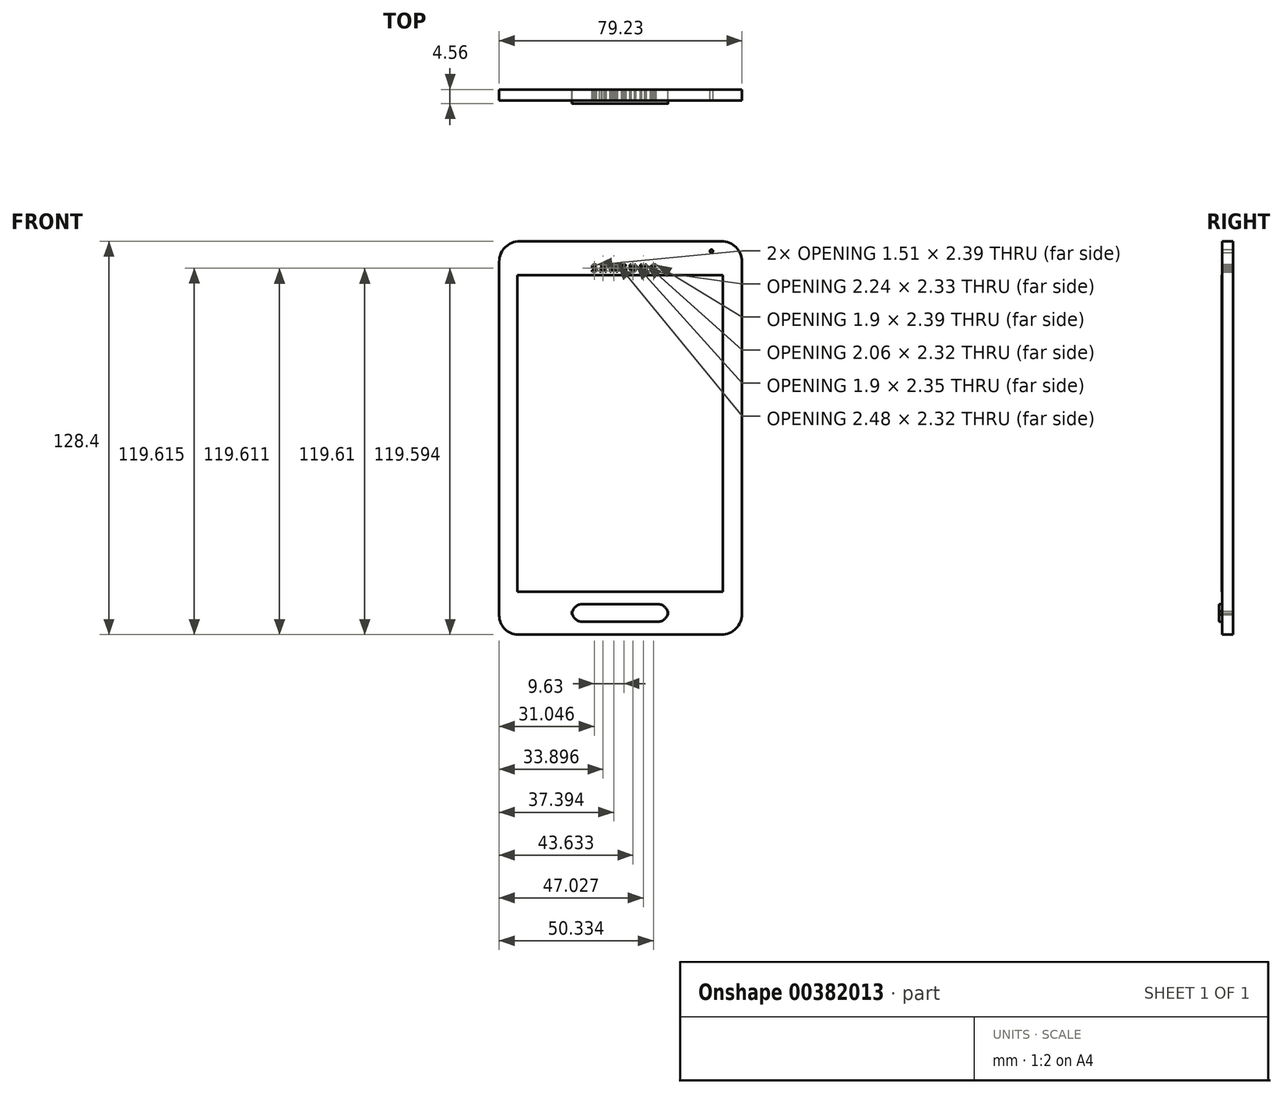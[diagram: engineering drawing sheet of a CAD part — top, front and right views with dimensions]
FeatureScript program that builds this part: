
annotation { "Feature Type Name" : "Feature", "Feature Type Description" : "" }
export const myFeature = defineFeature(function(context is Context, id is Id, definition is map)
    precondition{}
    {
        {
            var Q0;
            Q0=qCreatedBy(makeId("Front.planeOp"),FACE);
            var sketch = newSketch(context, id + "F0", { "sketchPlane" : qUnion([Q0])});
            skLineSegment(sketch, "E0.bottom", {"start": v(-53.86, 69.17) * mm, "end": v(11.97, 69.17) * mm});
            skLineSegment(sketch, "E0.top", {"start": v(-54.4, -59.23) * mm, "end": v(11.97, -59.23) * mm});
            skLineSegment(sketch, "E0.left", {"start": v(-60.56, 62.48) * mm, "end": v(-60.56, -53.06) * mm});
            skLineSegment(sketch, "E0.right", {"start": v(18.67, 62.48) * mm, "end": v(18.67, -52.53) * mm});
            skPoint(sketch, "E1.visualSharp", {"position": v(-60.56, 69.17) * mm});
            skArc(sketch, "E1.filletArc", {"start": v(-53.86, 69.17) * mm, "mid": v(-58.6, 67.21) * mm, "end": v(-60.56, 62.48) * mm});
            skPoint(sketch, "E2.visualSharp", {"position": v(18.67, 69.17) * mm});
            skArc(sketch, "E2.filletArc", {"start": v(18.67, 62.48) * mm, "mid": v(16.7, 67.21) * mm, "end": v(11.97, 69.17) * mm});
            skPoint(sketch, "E3.visualSharp", {"position": v(18.67, -59.23) * mm});
            skArc(sketch, "E3.filletArc", {"start": v(11.97, -59.23) * mm, "mid": v(16.7, -57.26) * mm, "end": v(18.67, -52.53) * mm});
            skPoint(sketch, "E4.visualSharp", {"position": v(-60.56, -59.23) * mm});
            skArc(sketch, "E4.filletArc", {"start": v(-60.56, -53.06) * mm, "mid": v(-58.75, -57.42) * mm, "end": v(-54.4, -59.23) * mm});
            skLineSegment(sketch, "E5", {"start": v(-54.67, 58.06) * mm, "end": v(12.46, 58.06) * mm});
            skLineSegment(sketch, "E6", {"start": v(12.46, 58.06) * mm, "end": v(12.46, -45.27) * mm});
            skLineSegment(sketch, "E7", {"start": v(12.46, -45.27) * mm, "end": v(-54.67, -45.27) * mm});
            skLineSegment(sketch, "E8", {"start": v(-54.67, -45.27) * mm, "end": v(-54.67, 58.06) * mm});
            skCircle(sketch, "E9", {"center": v(-47.07, 64.84) * mm, "radius": 1.65 * mm});
            skLineSegment(sketch, "E10.bottom", {"start": v(-28.87, 64.84) * mm, "end": v(-10.47, 64.84) * mm});
            skLineSegment(sketch, "E10.top", {"start": v(-28.77, 67.68) * mm, "end": v(-10.46, 67.68) * mm});
            skLineSegment(sketch, "E10.left", {"start": v(-29.78, 65.74) * mm, "end": v(-29.78, 66.67) * mm});
            skLineSegment(sketch, "E10.right", {"start": v(-9.55, 65.76) * mm, "end": v(-9.55, 66.78) * mm});
            skPoint(sketch, "E11.visualSharp", {"position": v(-29.78, 67.68) * mm});
            skArc(sketch, "E11.filletArc", {"start": v(-28.77, 67.68) * mm, "mid": v(-29.48, 67.39) * mm, "end": v(-29.78, 66.67) * mm});
            skPoint(sketch, "E12.visualSharp", {"position": v(-29.78, 64.84) * mm});
            skArc(sketch, "E12.filletArc", {"start": v(-29.78, 65.74) * mm, "mid": v(-29.51, 65.1) * mm, "end": v(-28.87, 64.84) * mm});
            skPoint(sketch, "E13.visualSharp", {"position": v(-9.55, 64.84) * mm});
            skArc(sketch, "E13.filletArc", {"start": v(-10.47, 64.84) * mm, "mid": v(-9.82, 65.1) * mm, "end": v(-9.55, 65.76) * mm});
            skPoint(sketch, "E14.visualSharp", {"position": v(-9.55, 67.68) * mm});
            skArc(sketch, "E14.filletArc", {"start": v(-9.55, 66.78) * mm, "mid": v(-9.82, 67.42) * mm, "end": v(-10.46, 67.68) * mm});
            skCircle(sketch, "E15", {"center": v(-3.77, 66.13) * mm, "radius": 1.09 * mm});
            skCircle(sketch, "E16", {"center": v(-0.62, 66.13) * mm, "radius": 1.1 * mm});
            skCircle(sketch, "E17", {"center": v(8.7, 65.95) * mm, "radius": 1.77 * mm});
            skCircle(sketch, "E18", {"center": v(8.7, 65.95) * mm, "radius": 0.51 * mm});
            skLineSegment(sketch, "E19.bottom", {"start": v(-33.35, -49.29) * mm, "end": v(-8.9, -49.29) * mm});
            skLineSegment(sketch, "E19.top", {"start": v(-33.35, -55.1) * mm, "end": v(-8.9, -55.1) * mm});
            skLineSegment(sketch, "E19.left", {"start": v(-36.82, -51.62) * mm, "end": v(-36.82, -52.76) * mm});
            skLineSegment(sketch, "E19.right", {"start": v(-5.44, -51.62) * mm, "end": v(-5.44, -52.76) * mm});
            skPoint(sketch, "E20.visualSharp", {"position": v(-36.82, -49.29) * mm});
            skArc(sketch, "E20.filletArc", {"start": v(-33.35, -49.29) * mm, "mid": v(-35.8, -50.3) * mm, "end": v(-36.82, -52.76) * mm});
            skPoint(sketch, "E21.visualSharp", {"position": v(-36.82, -55.1) * mm});
            skArc(sketch, "E21.filletArc", {"start": v(-36.82, -51.62) * mm, "mid": v(-35.8, -54.08) * mm, "end": v(-33.35, -55.1) * mm});
            skPoint(sketch, "E22.visualSharp", {"position": v(-5.44, -55.1) * mm});
            skArc(sketch, "E22.filletArc", {"start": v(-8.9, -55.1) * mm, "mid": v(-6.46, -54.08) * mm, "end": v(-5.44, -51.62) * mm});
            skPoint(sketch, "E23.visualSharp", {"position": v(-5.44, -49.29) * mm});
            skArc(sketch, "E23.filletArc", {"start": v(-5.44, -52.76) * mm, "mid": v(-6.46, -50.3) * mm, "end": v(-8.9, -49.29) * mm});
            skLineSegment(sketch, "E24.bottom", {"start": v(-55.14, -50.58) * mm, "end": v(-46.13, -50.58) * mm});
            skLineSegment(sketch, "E24.top", {"start": v(-55.14, -55.05) * mm, "end": v(-46.13, -55.05) * mm});
            skLineSegment(sketch, "E24.left", {"start": v(-55.14, -50.58) * mm, "end": v(-55.14, -55.05) * mm});
            skLineSegment(sketch, "E24.right", {"start": v(-46.13, -50.58) * mm, "end": v(-46.13, -55.05) * mm});
            skLineSegment(sketch, "E25", {"start": v(-50.67, -49.5) * mm, "end": v(-44.4, -49.5) * mm});
            skLineSegment(sketch, "E26", {"start": v(-44.4, -49.5) * mm, "end": v(-44.4, -54.04) * mm});
            skLineSegment(sketch, "E27", {"start": v(-44.4, -54.04) * mm, "end": v(-44.4, -49.5) * mm});
            skLineSegment(sketch, "E28", {"start": v(4.78, -54.93) * mm, "end": v(8.23, -54.93) * mm});
            skLineSegment(sketch, "E29", {"start": v(8.23, -54.93) * mm, "end": v(11.98, -54.93) * mm});
            skLineSegment(sketch, "E30", {"start": v(11.98, -54.93) * mm, "end": v(11.97, -52.53) * mm});
            skLineSegment(sketch, "E31", {"start": v(11.97, -50.8) * mm, "end": v(8.23, -50.8) * mm});
            skLineSegment(sketch, "E32", {"start": v(8.23, -50.8) * mm, "end": v(8.23, -49.07) * mm});
            skLineSegment(sketch, "E33", {"start": v(8.23, -49.07) * mm, "end": v(4.19, -50.54) * mm});
            skLineSegment(sketch, "E34", {"start": v(4.19, -50.54) * mm, "end": v(8.23, -52.53) * mm});
            skLineSegment(sketch, "E35", {"start": v(8.23, -52.53) * mm, "end": v(8.23, -50.8) * mm});
            skLineSegment(sketch, "E36", {"start": v(11.97, -50.8) * mm, "end": v(11.97, -52.53) * mm});
            skText(sketch, "E37", { "text": "S A M S U N G", "fontName": "OpenSans-Bold.ttf"});
            const initialGuessF0  = {"E37": [-0.03042, 0.05922, 1, 0, 0.00234]};
            skSetInitialGuess(sketch, initialGuessF0);
            skSolve(sketch);
        }
        {
            var Q0;
            Q0=makeQuery(id+"F0.imprint","IMPRINT",FACE,{"disambiguationData":[TD([[makeQuery(id+"F0.imprint","IMPRINT",EDGE,{"derivedFrom":sQuery(id+"F0.wireOp",EDGE,"E9")}),1.0]])]});
            var Q1;
            Q1=makeQuery(id+"F0.imprint","IMPRINT",FACE,{"disambiguationData":[TD([[makeQuery(id+"F0.imprint","IMPRINT",EDGE,{"derivedFrom":sQuery(id+"F0.wireOp",EDGE,"E10.bottom")}),1.0]])]});
            var Q2;
            {var subQ4=sQuery(id+"F0.wireOp",EDGE,"E19.bottom");Q2=makeQuery(id+"F0.imprint","IMPRINT",FACE,{"disambiguationData":[TD([[makeQuery(id+"F0.imprint","IMPRINT",EDGE,{"derivedFrom":subQ4}),-1.0]])]});}
            var Q3;
            Q3=makeQuery(id+"F0.imprint","IMPRINT",FACE,{"disambiguationData":[TD([[makeQuery(id+"F0.imprint","IMPRINT",EDGE,{"derivedFrom":sQuery(id+"F0.wireOp",EDGE,"E24.bottom")}),-1.0]])]});
            var Q4;
            Q4=makeQuery(id+"F0.imprint","IMPRINT",FACE,{"disambiguationData":[TD([[makeQuery(id+"F0.imprint","IMPRINT",EDGE,{"derivedFrom":sQuery(id+"F0.wireOp",EDGE,"E32")}),1.0]])]});
            var Q5;
            Q5=makeQuery(id+"F0.imprint","IMPRINT",FACE,{"disambiguationData":[TD([[makeQuery(id+"F0.imprint","IMPRINT",EDGE,{"derivedFrom":sQuery(id+"F0.wireOp",EDGE,"E15")}),1.0]])]});
            var Q6;
            Q6=makeQuery(id+"F0.imprint","IMPRINT",FACE,{"disambiguationData":[TD([[makeQuery(id+"F0.imprint","IMPRINT",EDGE,{"derivedFrom":sQuery(id+"F0.wireOp",EDGE,"E16")}),1.0]])]});
            var Q7;
            Q7=makeQuery(id+"F0.imprint","IMPRINT",FACE,{"disambiguationData":[TD([[makeQuery(id+"F0.imprint","IMPRINT",EDGE,{"derivedFrom":sQuery(id+"F0.wireOp",EDGE,"E17")}),1.0]])]});
            var Q8;
            Q8=makeQuery(id+"F0.imprint","IMPRINT",FACE,{"disambiguationData":[TD([[makeQuery(id+"F0.imprint","IMPRINT",EDGE,{"derivedFrom":sQuery(id+"F0.wireOp",EDGE,"E5")}),-1.0]])]});
            var Q9;
            Q9=makeQuery(id+"F0.imprint","IMPRINT",FACE,{"disambiguationData":[TD([[makeQuery(id+"F0.imprint","IMPRINT",EDGE,{"derivedFrom":sQuery(id+"F0.wireOp",EDGE,"E0.bottom")}),-1.0]])]});
            extrude(context, id + "F1", {"entities" : qUnion([Q0, Q1, Q2, Q3, Q4, Q5, Q6, Q7, Q8, Q9]), "depth" : 3.56 * mm});
        }
        {
            var Q0;
            Q0=makeQuery(id+"F1.opExtrude","CAP_FACE",FACE,{"disambiguationData":[OSD([sQuery(id+"F0.wireOp",EDGE,"E0.bottom"),sQuery(id+"F0.wireOp",EDGE,"E0.top"),sQuery(id+"F0.wireOp",EDGE,"E0.left"),sQuery(id+"F0.wireOp",EDGE,"E0.right"),sQuery(id+"F0.wireOp",EDGE,"E1.filletArc"),sQuery(id+"F0.wireOp",EDGE,"E2.filletArc"),sQuery(id+"F0.wireOp",EDGE,"E3.filletArc"),sQuery(id+"F0.wireOp",EDGE,"E4.filletArc"),sQuery(id+"F0.wireOp",EDGE,"E18"),sQuery(id+"F0.wireOp",EDGE,"E19.left"),sQuery(id+"F0.wireOp",EDGE,"E19.right"),sQuery(id+"F0.wireOp",EDGE,"E20.filletArc"),sQuery(id+"F0.wireOp",EDGE,"E21.filletArc"),sQuery(id+"F0.wireOp",EDGE,"E22.filletArc"),sQuery(id+"F0.wireOp",EDGE,"E23.filletArc"),sQuery(id+"F0.wireOp",EDGE,"E37.sketch_text.stroke-0"),sQuery(id+"F0.wireOp",EDGE,"E37.sketch_text.stroke-1"),sQuery(id+"F0.wireOp",EDGE,"E37.sketch_text.stroke-2"),sQuery(id+"F0.wireOp",EDGE,"E37.sketch_text.stroke-3"),sQuery(id+"F0.wireOp",EDGE,"E37.sketch_text.stroke-4"),sQuery(id+"F0.wireOp",EDGE,"E37.sketch_text.stroke-5"),sQuery(id+"F0.wireOp",EDGE,"E37.sketch_text.stroke-6"),sQuery(id+"F0.wireOp",EDGE,"E37.sketch_text.stroke-7"),sQuery(id+"F0.wireOp",EDGE,"E37.sketch_text.stroke-8"),sQuery(id+"F0.wireOp",EDGE,"E37.sketch_text.stroke-9"),sQuery(id+"F0.wireOp",EDGE,"E37.sketch_text.stroke-10"),sQuery(id+"F0.wireOp",EDGE,"E37.sketch_text.stroke-11"),sQuery(id+"F0.wireOp",EDGE,"E37.sketch_text.stroke-12"),sQuery(id+"F0.wireOp",EDGE,"E37.sketch_text.stroke-13"),sQuery(id+"F0.wireOp",EDGE,"E37.sketch_text.stroke-14"),sQuery(id+"F0.wireOp",EDGE,"E37.sketch_text.stroke-15"),sQuery(id+"F0.wireOp",EDGE,"E37.sketch_text.stroke-16"),sQuery(id+"F0.wireOp",EDGE,"E37.sketch_text.stroke-17"),sQuery(id+"F0.wireOp",EDGE,"E37.sketch_text.stroke-18"),sQuery(id+"F0.wireOp",EDGE,"E37.sketch_text.stroke-19"),sQuery(id+"F0.wireOp",EDGE,"E37.sketch_text.stroke-20"),sQuery(id+"F0.wireOp",EDGE,"E37.sketch_text.stroke-21"),sQuery(id+"F0.wireOp",EDGE,"E37.sketch_text.stroke-22"),sQuery(id+"F0.wireOp",EDGE,"E37.sketch_text.stroke-23"),sQuery(id+"F0.wireOp",EDGE,"E37.sketch_text.stroke-24"),sQuery(id+"F0.wireOp",EDGE,"E37.sketch_text.stroke-25"),sQuery(id+"F0.wireOp",EDGE,"E37.sketch_text.stroke-26"),sQuery(id+"F0.wireOp",EDGE,"E37.sketch_text.stroke-27"),sQuery(id+"F0.wireOp",EDGE,"E37.sketch_text.stroke-28"),sQuery(id+"F0.wireOp",EDGE,"E37.sketch_text.stroke-29"),sQuery(id+"F0.wireOp",EDGE,"E37.sketch_text.stroke-30"),sQuery(id+"F0.wireOp",EDGE,"E37.sketch_text.stroke-31"),sQuery(id+"F0.wireOp",EDGE,"E37.sketch_text.stroke-32"),sQuery(id+"F0.wireOp",EDGE,"E37.sketch_text.stroke-33"),sQuery(id+"F0.wireOp",EDGE,"E37.sketch_text.stroke-34"),sQuery(id+"F0.wireOp",EDGE,"E37.sketch_text.stroke-35"),sQuery(id+"F0.wireOp",EDGE,"E37.sketch_text.stroke-40"),sQuery(id+"F0.wireOp",EDGE,"E37.sketch_text.stroke-41"),sQuery(id+"F0.wireOp",EDGE,"E37.sketch_text.stroke-42"),sQuery(id+"F0.wireOp",EDGE,"E37.sketch_text.stroke-43"),sQuery(id+"F0.wireOp",EDGE,"E37.sketch_text.stroke-44"),sQuery(id+"F0.wireOp",EDGE,"E37.sketch_text.stroke-45"),sQuery(id+"F0.wireOp",EDGE,"E37.sketch_text.stroke-46"),sQuery(id+"F0.wireOp",EDGE,"E37.sketch_text.stroke-47"),sQuery(id+"F0.wireOp",EDGE,"E37.sketch_text.stroke-48"),sQuery(id+"F0.wireOp",EDGE,"E37.sketch_text.stroke-49"),sQuery(id+"F0.wireOp",EDGE,"E37.sketch_text.stroke-50"),sQuery(id+"F0.wireOp",EDGE,"E37.sketch_text.stroke-51"),sQuery(id+"F0.wireOp",EDGE,"E37.sketch_text.stroke-52"),sQuery(id+"F0.wireOp",EDGE,"E37.sketch_text.stroke-53"),sQuery(id+"F0.wireOp",EDGE,"E37.sketch_text.stroke-54"),sQuery(id+"F0.wireOp",EDGE,"E37.sketch_text.stroke-55"),sQuery(id+"F0.wireOp",EDGE,"E37.sketch_text.stroke-56"),sQuery(id+"F0.wireOp",EDGE,"E37.sketch_text.stroke-57"),sQuery(id+"F0.wireOp",EDGE,"E37.sketch_text.stroke-58"),sQuery(id+"F0.wireOp",EDGE,"E37.sketch_text.stroke-59"),sQuery(id+"F0.wireOp",EDGE,"E37.sketch_text.stroke-60"),sQuery(id+"F0.wireOp",EDGE,"E37.sketch_text.stroke-61"),sQuery(id+"F0.wireOp",EDGE,"E37.sketch_text.stroke-62"),sQuery(id+"F0.wireOp",EDGE,"E37.sketch_text.stroke-63"),sQuery(id+"F0.wireOp",EDGE,"E37.sketch_text.stroke-64"),sQuery(id+"F0.wireOp",EDGE,"E37.sketch_text.stroke-65"),sQuery(id+"F0.wireOp",EDGE,"E37.sketch_text.stroke-66"),sQuery(id+"F0.wireOp",EDGE,"E37.sketch_text.stroke-67"),sQuery(id+"F0.wireOp",EDGE,"E37.sketch_text.stroke-68"),sQuery(id+"F0.wireOp",EDGE,"E37.sketch_text.stroke-69"),sQuery(id+"F0.wireOp",EDGE,"E37.sketch_text.stroke-70"),sQuery(id+"F0.wireOp",EDGE,"E37.sketch_text.stroke-71"),sQuery(id+"F0.wireOp",EDGE,"E37.sketch_text.stroke-72"),sQuery(id+"F0.wireOp",EDGE,"E37.sketch_text.stroke-73"),sQuery(id+"F0.wireOp",EDGE,"E37.sketch_text.stroke-74"),sQuery(id+"F0.wireOp",EDGE,"E37.sketch_text.stroke-75"),sQuery(id+"F0.wireOp",EDGE,"E37.sketch_text.stroke-76"),sQuery(id+"F0.wireOp",EDGE,"E37.sketch_text.stroke-77"),sQuery(id+"F0.wireOp",EDGE,"E37.sketch_text.stroke-78"),sQuery(id+"F0.wireOp",EDGE,"E37.sketch_text.stroke-79"),sQuery(id+"F0.wireOp",EDGE,"E37.sketch_text.stroke-80"),sQuery(id+"F0.wireOp",EDGE,"E37.sketch_text.stroke-81"),sQuery(id+"F0.wireOp",EDGE,"E37.sketch_text.stroke-82"),sQuery(id+"F0.wireOp",EDGE,"E37.sketch_text.stroke-83"),sQuery(id+"F0.wireOp",EDGE,"E37.sketch_text.stroke-84"),sQuery(id+"F0.wireOp",EDGE,"E37.sketch_text.stroke-85"),sQuery(id+"F0.wireOp",EDGE,"E37.sketch_text.stroke-86"),sQuery(id+"F0.wireOp",EDGE,"E37.sketch_text.stroke-87"),sQuery(id+"F0.wireOp",EDGE,"E37.sketch_text.stroke-88"),sQuery(id+"F0.wireOp",EDGE,"E37.sketch_text.stroke-89"),sQuery(id+"F0.wireOp",EDGE,"E37.sketch_text.stroke-90"),sQuery(id+"F0.wireOp",EDGE,"E37.sketch_text.stroke-91"),sQuery(id+"F0.wireOp",EDGE,"E37.sketch_text.stroke-92"),sQuery(id+"F0.wireOp",EDGE,"E37.sketch_text.stroke-93"),sQuery(id+"F0.wireOp",EDGE,"E37.sketch_text.stroke-94"),sQuery(id+"F0.wireOp",EDGE,"E37.sketch_text.stroke-95"),sQuery(id+"F0.wireOp",EDGE,"E37.sketch_text.stroke-96"),sQuery(id+"F0.wireOp",EDGE,"E37.sketch_text.stroke-97"),sQuery(id+"F0.wireOp",EDGE,"E37.sketch_text.stroke-98"),sQuery(id+"F0.wireOp",EDGE,"E37.sketch_text.stroke-99"),sQuery(id+"F0.wireOp",EDGE,"E37.sketch_text.stroke-100"),sQuery(id+"F0.wireOp",EDGE,"E37.sketch_text.stroke-101"),sQuery(id+"F0.wireOp",EDGE,"E37.sketch_text.stroke-102"),sQuery(id+"F0.wireOp",EDGE,"E37.sketch_text.stroke-103"),sQuery(id+"F0.wireOp",EDGE,"E37.sketch_text.stroke-104"),sQuery(id+"F0.wireOp",EDGE,"E37.sketch_text.stroke-105"),sQuery(id+"F0.wireOp",EDGE,"E37.sketch_text.stroke-106"),sQuery(id+"F0.wireOp",EDGE,"E37.sketch_text.stroke-107"),sQuery(id+"F0.wireOp",EDGE,"E37.sketch_text.stroke-108"),sQuery(id+"F0.wireOp",EDGE,"E37.sketch_text.stroke-109"),sQuery(id+"F0.wireOp",EDGE,"E37.sketch_text.stroke-110"),sQuery(id+"F0.wireOp",EDGE,"E37.sketch_text.stroke-111"),sQuery(id+"F0.wireOp",EDGE,"E37.sketch_text.stroke-112"),sQuery(id+"F0.wireOp",EDGE,"E37.sketch_text.stroke-113"),sQuery(id+"F0.wireOp",EDGE,"E37.sketch_text.stroke-114"),sQuery(id+"F0.wireOp",EDGE,"E37.sketch_text.stroke-115"),sQuery(id+"F0.wireOp",EDGE,"E37.sketch_text.stroke-116"),sQuery(id+"F0.wireOp",EDGE,"E37.sketch_text.stroke-117"),sQuery(id+"F0.wireOp",EDGE,"E37.sketch_text.stroke-118"),sQuery(id+"F0.wireOp",EDGE,"E37.sketch_text.stroke-119"),sQuery(id+"F0.wireOp",EDGE,"E37.sketch_text.stroke-120"),sQuery(id+"F0.wireOp",EDGE,"E37.sketch_text.stroke-121"),sQuery(id+"F0.wireOp",EDGE,"E37.sketch_text.stroke-122"),sQuery(id+"F0.wireOp",EDGE,"E37.sketch_text.stroke-123"),sQuery(id+"F0.wireOp",EDGE,"E37.sketch_text.stroke-124"),sQuery(id+"F0.wireOp",EDGE,"E37.sketch_text.stroke-125"),sQuery(id+"F0.wireOp",EDGE,"E37.sketch_text.stroke-126"),sQuery(id+"F0.wireOp",EDGE,"E37.sketch_text.stroke-127"),sQuery(id+"F0.wireOp",EDGE,"E37.sketch_text.stroke-128"),sQuery(id+"F0.wireOp",EDGE,"E37.sketch_text.stroke-129"),sQuery(id+"F0.wireOp",EDGE,"E37.sketch_text.stroke-130"),sQuery(id+"F0.wireOp",EDGE,"E37.sketch_text.stroke-131"),sQuery(id+"F0.wireOp",EDGE,"E37.sketch_text.stroke-132"),sQuery(id+"F0.wireOp",EDGE,"E37.sketch_text.stroke-133"),sQuery(id+"F0.wireOp",EDGE,"E37.sketch_text.stroke-134")])],"isStart":false});
            var sketch = newSketch(context, id + "F2", { "sketchPlane" : qUnion([Q0])});
            skLineSegment(sketch, "E38.bottom", {"start": v(-33.35, -49.29) * mm, "end": v(-8.9, -49.29) * mm});
            skLineSegment(sketch, "E38.top", {"start": v(-33.35, -55.1) * mm, "end": v(-8.9, -55.1) * mm});
            skLineSegment(sketch, "E38.left", {"start": v(-36.82, -51.62) * mm, "end": v(-36.82, -52.76) * mm});
            skLineSegment(sketch, "E38.right", {"start": v(-5.44, -51.62) * mm, "end": v(-5.44, -52.76) * mm});
            skPoint(sketch, "E39.visualSharp", {"position": v(-36.82, -49.29) * mm});
            skArc(sketch, "E39.filletArc", {"start": v(-33.35, -49.29) * mm, "mid": v(-35.8, -50.3) * mm, "end": v(-36.82, -52.76) * mm});
            skPoint(sketch, "E40.visualSharp", {"position": v(-36.82, -55.1) * mm});
            skArc(sketch, "E40.filletArc", {"start": v(-36.82, -51.62) * mm, "mid": v(-35.8, -54.08) * mm, "end": v(-33.35, -55.1) * mm});
            skPoint(sketch, "E41.visualSharp", {"position": v(-5.44, -55.1) * mm});
            skArc(sketch, "E41.filletArc", {"start": v(-8.9, -55.1) * mm, "mid": v(-6.46, -54.08) * mm, "end": v(-5.44, -51.62) * mm});
            skPoint(sketch, "E42.visualSharp", {"position": v(-5.44, -49.29) * mm});
            skArc(sketch, "E42.filletArc", {"start": v(-5.44, -52.76) * mm, "mid": v(-6.46, -50.3) * mm, "end": v(-8.9, -49.29) * mm});
            skSolve(sketch);
        }
        {
            var Q0;
            Q0 = qSketchRegion(id + "F2", true);
            extrude(context, id + "F3", {"entities" : qUnion([Q0]), "depth" : 1 * mm});
        }
        {
            var Q0;
            Q0=makeQuery(id+"F1.opExtrude","CAP_FACE",FACE,{"disambiguationData":[OSD([sQuery(id+"F0.wireOp",EDGE,"E0.bottom"),sQuery(id+"F0.wireOp",EDGE,"E0.top"),sQuery(id+"F0.wireOp",EDGE,"E0.left"),sQuery(id+"F0.wireOp",EDGE,"E0.right"),sQuery(id+"F0.wireOp",EDGE,"E1.filletArc"),sQuery(id+"F0.wireOp",EDGE,"E2.filletArc"),sQuery(id+"F0.wireOp",EDGE,"E3.filletArc"),sQuery(id+"F0.wireOp",EDGE,"E4.filletArc"),sQuery(id+"F0.wireOp",EDGE,"E18"),sQuery(id+"F0.wireOp",EDGE,"E19.left"),sQuery(id+"F0.wireOp",EDGE,"E19.right"),sQuery(id+"F0.wireOp",EDGE,"E20.filletArc"),sQuery(id+"F0.wireOp",EDGE,"E21.filletArc"),sQuery(id+"F0.wireOp",EDGE,"E22.filletArc"),sQuery(id+"F0.wireOp",EDGE,"E23.filletArc"),sQuery(id+"F0.wireOp",EDGE,"E37.sketch_text.stroke-0"),sQuery(id+"F0.wireOp",EDGE,"E37.sketch_text.stroke-1"),sQuery(id+"F0.wireOp",EDGE,"E37.sketch_text.stroke-2"),sQuery(id+"F0.wireOp",EDGE,"E37.sketch_text.stroke-3"),sQuery(id+"F0.wireOp",EDGE,"E37.sketch_text.stroke-4"),sQuery(id+"F0.wireOp",EDGE,"E37.sketch_text.stroke-5"),sQuery(id+"F0.wireOp",EDGE,"E37.sketch_text.stroke-6"),sQuery(id+"F0.wireOp",EDGE,"E37.sketch_text.stroke-7"),sQuery(id+"F0.wireOp",EDGE,"E37.sketch_text.stroke-8"),sQuery(id+"F0.wireOp",EDGE,"E37.sketch_text.stroke-9"),sQuery(id+"F0.wireOp",EDGE,"E37.sketch_text.stroke-10"),sQuery(id+"F0.wireOp",EDGE,"E37.sketch_text.stroke-11"),sQuery(id+"F0.wireOp",EDGE,"E37.sketch_text.stroke-12"),sQuery(id+"F0.wireOp",EDGE,"E37.sketch_text.stroke-13"),sQuery(id+"F0.wireOp",EDGE,"E37.sketch_text.stroke-14"),sQuery(id+"F0.wireOp",EDGE,"E37.sketch_text.stroke-15"),sQuery(id+"F0.wireOp",EDGE,"E37.sketch_text.stroke-16"),sQuery(id+"F0.wireOp",EDGE,"E37.sketch_text.stroke-17"),sQuery(id+"F0.wireOp",EDGE,"E37.sketch_text.stroke-18"),sQuery(id+"F0.wireOp",EDGE,"E37.sketch_text.stroke-19"),sQuery(id+"F0.wireOp",EDGE,"E37.sketch_text.stroke-20"),sQuery(id+"F0.wireOp",EDGE,"E37.sketch_text.stroke-21"),sQuery(id+"F0.wireOp",EDGE,"E37.sketch_text.stroke-22"),sQuery(id+"F0.wireOp",EDGE,"E37.sketch_text.stroke-23"),sQuery(id+"F0.wireOp",EDGE,"E37.sketch_text.stroke-24"),sQuery(id+"F0.wireOp",EDGE,"E37.sketch_text.stroke-25"),sQuery(id+"F0.wireOp",EDGE,"E37.sketch_text.stroke-26"),sQuery(id+"F0.wireOp",EDGE,"E37.sketch_text.stroke-27"),sQuery(id+"F0.wireOp",EDGE,"E37.sketch_text.stroke-28"),sQuery(id+"F0.wireOp",EDGE,"E37.sketch_text.stroke-29"),sQuery(id+"F0.wireOp",EDGE,"E37.sketch_text.stroke-30"),sQuery(id+"F0.wireOp",EDGE,"E37.sketch_text.stroke-31"),sQuery(id+"F0.wireOp",EDGE,"E37.sketch_text.stroke-32"),sQuery(id+"F0.wireOp",EDGE,"E37.sketch_text.stroke-33"),sQuery(id+"F0.wireOp",EDGE,"E37.sketch_text.stroke-34"),sQuery(id+"F0.wireOp",EDGE,"E37.sketch_text.stroke-35"),sQuery(id+"F0.wireOp",EDGE,"E37.sketch_text.stroke-40"),sQuery(id+"F0.wireOp",EDGE,"E37.sketch_text.stroke-41"),sQuery(id+"F0.wireOp",EDGE,"E37.sketch_text.stroke-42"),sQuery(id+"F0.wireOp",EDGE,"E37.sketch_text.stroke-43"),sQuery(id+"F0.wireOp",EDGE,"E37.sketch_text.stroke-44"),sQuery(id+"F0.wireOp",EDGE,"E37.sketch_text.stroke-45"),sQuery(id+"F0.wireOp",EDGE,"E37.sketch_text.stroke-46"),sQuery(id+"F0.wireOp",EDGE,"E37.sketch_text.stroke-47"),sQuery(id+"F0.wireOp",EDGE,"E37.sketch_text.stroke-48"),sQuery(id+"F0.wireOp",EDGE,"E37.sketch_text.stroke-49"),sQuery(id+"F0.wireOp",EDGE,"E37.sketch_text.stroke-50"),sQuery(id+"F0.wireOp",EDGE,"E37.sketch_text.stroke-51"),sQuery(id+"F0.wireOp",EDGE,"E37.sketch_text.stroke-52"),sQuery(id+"F0.wireOp",EDGE,"E37.sketch_text.stroke-53"),sQuery(id+"F0.wireOp",EDGE,"E37.sketch_text.stroke-54"),sQuery(id+"F0.wireOp",EDGE,"E37.sketch_text.stroke-55"),sQuery(id+"F0.wireOp",EDGE,"E37.sketch_text.stroke-56"),sQuery(id+"F0.wireOp",EDGE,"E37.sketch_text.stroke-57"),sQuery(id+"F0.wireOp",EDGE,"E37.sketch_text.stroke-58"),sQuery(id+"F0.wireOp",EDGE,"E37.sketch_text.stroke-59"),sQuery(id+"F0.wireOp",EDGE,"E37.sketch_text.stroke-60"),sQuery(id+"F0.wireOp",EDGE,"E37.sketch_text.stroke-61"),sQuery(id+"F0.wireOp",EDGE,"E37.sketch_text.stroke-62"),sQuery(id+"F0.wireOp",EDGE,"E37.sketch_text.stroke-63"),sQuery(id+"F0.wireOp",EDGE,"E37.sketch_text.stroke-64"),sQuery(id+"F0.wireOp",EDGE,"E37.sketch_text.stroke-65"),sQuery(id+"F0.wireOp",EDGE,"E37.sketch_text.stroke-66"),sQuery(id+"F0.wireOp",EDGE,"E37.sketch_text.stroke-67"),sQuery(id+"F0.wireOp",EDGE,"E37.sketch_text.stroke-68"),sQuery(id+"F0.wireOp",EDGE,"E37.sketch_text.stroke-69"),sQuery(id+"F0.wireOp",EDGE,"E37.sketch_text.stroke-70"),sQuery(id+"F0.wireOp",EDGE,"E37.sketch_text.stroke-71"),sQuery(id+"F0.wireOp",EDGE,"E37.sketch_text.stroke-72"),sQuery(id+"F0.wireOp",EDGE,"E37.sketch_text.stroke-73"),sQuery(id+"F0.wireOp",EDGE,"E37.sketch_text.stroke-74"),sQuery(id+"F0.wireOp",EDGE,"E37.sketch_text.stroke-75"),sQuery(id+"F0.wireOp",EDGE,"E37.sketch_text.stroke-76"),sQuery(id+"F0.wireOp",EDGE,"E37.sketch_text.stroke-77"),sQuery(id+"F0.wireOp",EDGE,"E37.sketch_text.stroke-78"),sQuery(id+"F0.wireOp",EDGE,"E37.sketch_text.stroke-79"),sQuery(id+"F0.wireOp",EDGE,"E37.sketch_text.stroke-80"),sQuery(id+"F0.wireOp",EDGE,"E37.sketch_text.stroke-81"),sQuery(id+"F0.wireOp",EDGE,"E37.sketch_text.stroke-82"),sQuery(id+"F0.wireOp",EDGE,"E37.sketch_text.stroke-83"),sQuery(id+"F0.wireOp",EDGE,"E37.sketch_text.stroke-84"),sQuery(id+"F0.wireOp",EDGE,"E37.sketch_text.stroke-85"),sQuery(id+"F0.wireOp",EDGE,"E37.sketch_text.stroke-86"),sQuery(id+"F0.wireOp",EDGE,"E37.sketch_text.stroke-87"),sQuery(id+"F0.wireOp",EDGE,"E37.sketch_text.stroke-88"),sQuery(id+"F0.wireOp",EDGE,"E37.sketch_text.stroke-89"),sQuery(id+"F0.wireOp",EDGE,"E37.sketch_text.stroke-90"),sQuery(id+"F0.wireOp",EDGE,"E37.sketch_text.stroke-91"),sQuery(id+"F0.wireOp",EDGE,"E37.sketch_text.stroke-92"),sQuery(id+"F0.wireOp",EDGE,"E37.sketch_text.stroke-93"),sQuery(id+"F0.wireOp",EDGE,"E37.sketch_text.stroke-94"),sQuery(id+"F0.wireOp",EDGE,"E37.sketch_text.stroke-95"),sQuery(id+"F0.wireOp",EDGE,"E37.sketch_text.stroke-96"),sQuery(id+"F0.wireOp",EDGE,"E37.sketch_text.stroke-97"),sQuery(id+"F0.wireOp",EDGE,"E37.sketch_text.stroke-98"),sQuery(id+"F0.wireOp",EDGE,"E37.sketch_text.stroke-99"),sQuery(id+"F0.wireOp",EDGE,"E37.sketch_text.stroke-100"),sQuery(id+"F0.wireOp",EDGE,"E37.sketch_text.stroke-101"),sQuery(id+"F0.wireOp",EDGE,"E37.sketch_text.stroke-102"),sQuery(id+"F0.wireOp",EDGE,"E37.sketch_text.stroke-103"),sQuery(id+"F0.wireOp",EDGE,"E37.sketch_text.stroke-104"),sQuery(id+"F0.wireOp",EDGE,"E37.sketch_text.stroke-105"),sQuery(id+"F0.wireOp",EDGE,"E37.sketch_text.stroke-106"),sQuery(id+"F0.wireOp",EDGE,"E37.sketch_text.stroke-107"),sQuery(id+"F0.wireOp",EDGE,"E37.sketch_text.stroke-108"),sQuery(id+"F0.wireOp",EDGE,"E37.sketch_text.stroke-109"),sQuery(id+"F0.wireOp",EDGE,"E37.sketch_text.stroke-110"),sQuery(id+"F0.wireOp",EDGE,"E37.sketch_text.stroke-111"),sQuery(id+"F0.wireOp",EDGE,"E37.sketch_text.stroke-112"),sQuery(id+"F0.wireOp",EDGE,"E37.sketch_text.stroke-113"),sQuery(id+"F0.wireOp",EDGE,"E37.sketch_text.stroke-114"),sQuery(id+"F0.wireOp",EDGE,"E37.sketch_text.stroke-115"),sQuery(id+"F0.wireOp",EDGE,"E37.sketch_text.stroke-116"),sQuery(id+"F0.wireOp",EDGE,"E37.sketch_text.stroke-117"),sQuery(id+"F0.wireOp",EDGE,"E37.sketch_text.stroke-118"),sQuery(id+"F0.wireOp",EDGE,"E37.sketch_text.stroke-119"),sQuery(id+"F0.wireOp",EDGE,"E37.sketch_text.stroke-120"),sQuery(id+"F0.wireOp",EDGE,"E37.sketch_text.stroke-121"),sQuery(id+"F0.wireOp",EDGE,"E37.sketch_text.stroke-122"),sQuery(id+"F0.wireOp",EDGE,"E37.sketch_text.stroke-123"),sQuery(id+"F0.wireOp",EDGE,"E37.sketch_text.stroke-124"),sQuery(id+"F0.wireOp",EDGE,"E37.sketch_text.stroke-125"),sQuery(id+"F0.wireOp",EDGE,"E37.sketch_text.stroke-126"),sQuery(id+"F0.wireOp",EDGE,"E37.sketch_text.stroke-127"),sQuery(id+"F0.wireOp",EDGE,"E37.sketch_text.stroke-128"),sQuery(id+"F0.wireOp",EDGE,"E37.sketch_text.stroke-129"),sQuery(id+"F0.wireOp",EDGE,"E37.sketch_text.stroke-130"),sQuery(id+"F0.wireOp",EDGE,"E37.sketch_text.stroke-131"),sQuery(id+"F0.wireOp",EDGE,"E37.sketch_text.stroke-132"),sQuery(id+"F0.wireOp",EDGE,"E37.sketch_text.stroke-133"),sQuery(id+"F0.wireOp",EDGE,"E37.sketch_text.stroke-134")])],"isStart":false});
            var sketch = newSketch(context, id + "F4", { "sketchPlane" : qUnion([Q0])});
            skLineSegment(sketch, "E43", {"start": v(-54.67, 58.06) * mm, "end": v(12.46, 58.06) * mm});
            skLineSegment(sketch, "E44", {"start": v(12.46, 58.06) * mm, "end": v(12.46, -45.27) * mm});
            skLineSegment(sketch, "E45", {"start": v(12.46, -45.27) * mm, "end": v(-54.67, -45.27) * mm});
            skLineSegment(sketch, "E46", {"start": v(-54.67, -45.27) * mm, "end": v(-54.67, 58.06) * mm});
            skSolve(sketch);
        }
        {
            var Q0;
            Q0 = qSketchRegion(id + "F4", true);
            var Q1;
            Q1 = qConstructionFilter(qBodyType(qCreatedBy(id + "F4" ,EDGE), BodyType.WIRE), ConstructionObject.NO);
            extrude(context, id + "F5", {"entities" : qUnion([Q0]), "surfaceEntities" : qUnion([Q1]), "depth" : 0.1 * mm});
        }
    });
